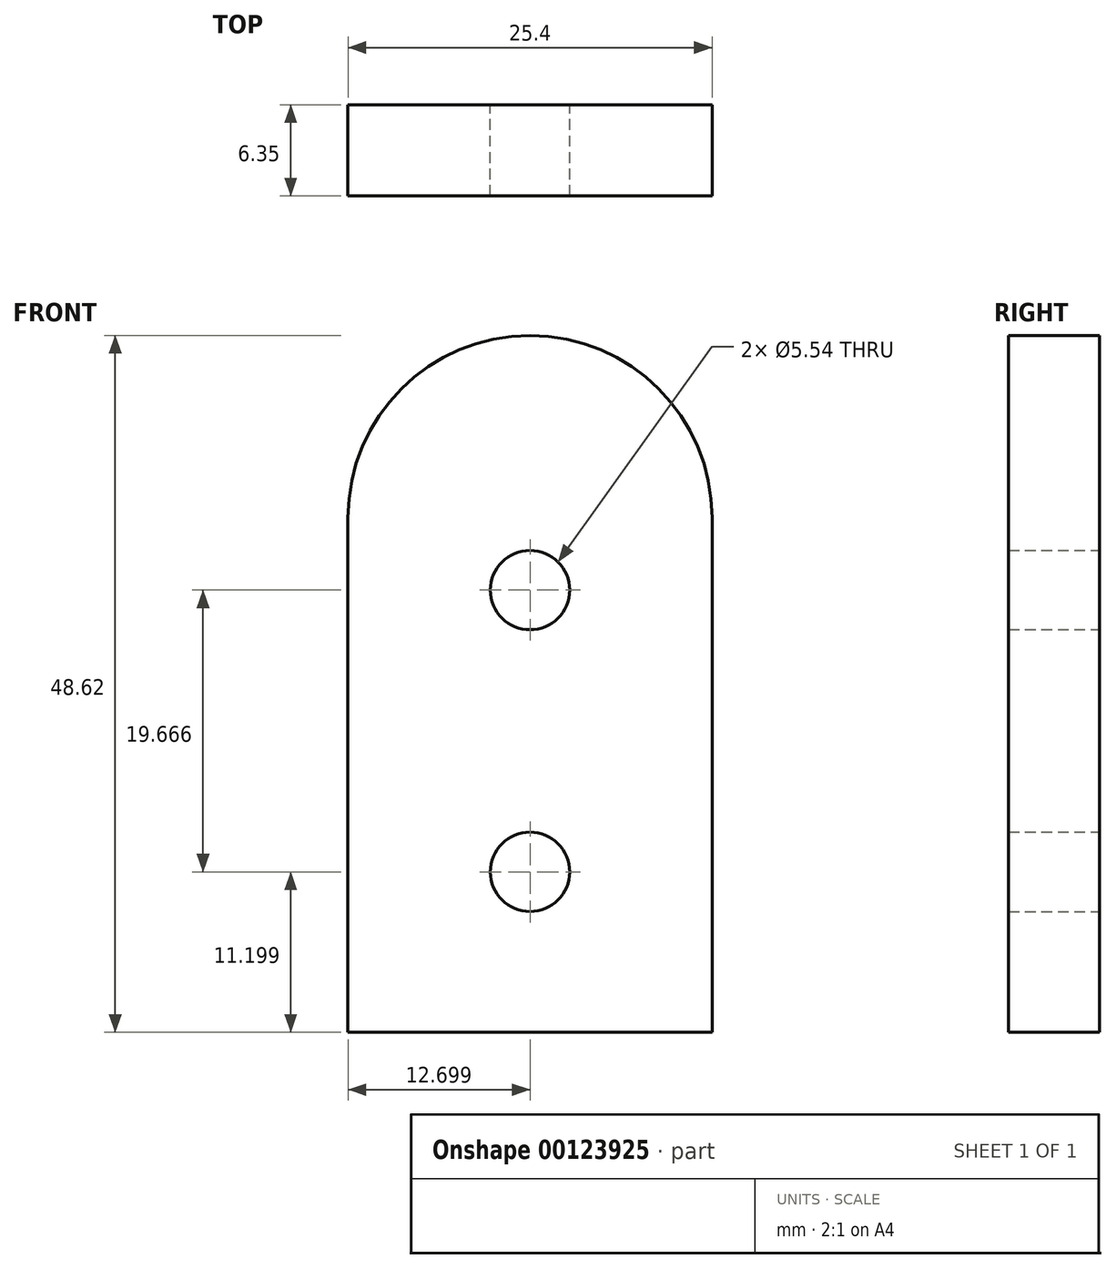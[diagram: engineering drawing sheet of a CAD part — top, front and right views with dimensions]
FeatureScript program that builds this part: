
annotation { "Feature Type Name" : "Feature", "Feature Type Description" : "" }
export const myFeature = defineFeature(function(context is Context, id is Id, definition is map)
    precondition{}
    {
        {
            var Q0;
            Q0=qCreatedBy(makeId("Front.planeOp"),FACE);
            var sketch = newSketch(context, id + "F0", { "sketchPlane" : qUnion([Q0])});
            skLineSegment(sketch, "E0", {"start": v(-44.1, 0) * mm, "end": v(-44.1, 35.92) * mm});
            skLineSegment(sketch, "E1", {"start": v(-18.7, 0) * mm, "end": v(-18.7, 35.92) * mm});
            skArc(sketch, "E2", {"start": v(-18.7, 35.92) * mm, "mid": v(-31.4, 48.62) * mm, "end": v(-44.1, 35.92) * mm});
            skLineSegment(sketch, "E3", {"start": v(-44.1, 0) * mm, "end": v(-18.7, 0) * mm});
            skPoint(sketch, "E4.startSnap0", {"position": v(-31.4, 0) * mm});
            skLineSegment(sketch, "E5", {"start": v(-31.4, 0) * mm, "end": v(-31.4, 48.62) * mm});
            skCircle(sketch, "E6", {"center": v(-31.4, 30.86) * mm, "radius": 2.77 * mm});
            skCircle(sketch, "E7", {"center": v(-31.4, 11.2) * mm, "radius": 2.77 * mm});
            skLineSegment(sketch, "E8", {"start": v(0, 56.27) * mm, "end": v(0, 0) * mm});
            skSolve(sketch);
        }
        {
            var Q0;
            Q0 = qSketchRegion(id + "F0", true);
            extrude(context, id + "F1", {"entities" : qUnion([Q0]), "depth" : 6.35 * mm});
        }
    });
